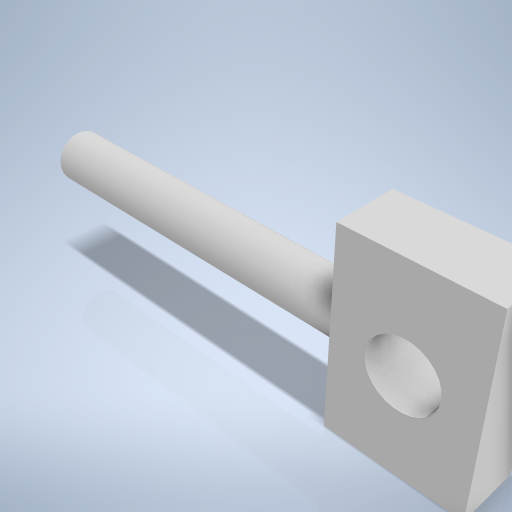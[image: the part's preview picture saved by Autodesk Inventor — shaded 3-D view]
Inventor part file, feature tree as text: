
AUTODESK INVENTOR PART (.ipt)
format: ipt  version: 2024.2 (Build 282272000, 272)  size: 252,416 bytes
history: native  units: mm
features: sketch x4, extrude x2, hole x2
ambient origin geometry x8: Origin, YZ Plane, XZ Plane, XY Plane, X Axis, Y Axis, Z Axis, Center Point
bodies: Volumenkörper1 (feature_tree)
feature tree (8):
  extrude  "Extrusion1"  Depth=13.0mm
  hole  "Bohrung1"  [1 undecoded]
  extrude  "Extrusion2"  [1 undecoded]
  hole  "Bohrung2"  [1 undecoded]
  sketch  "Skizze2"  dims[d1=19.0mm d2=13.0mm]
  sketch  "Skizze3"  dims[d3=6.0mm d4=0.0mm]
  sketch  "Skizze4"  dims[d5=6.5mm d6=8.0mm d7=4.0mm d8=2.0mm d9=90.0deg d10=15.75mm d11=20.594885mm d12=5.0mm]
  sketch  "Skizze5"  dims[d13=34.0mm d14=0.0mm d15=3.242mm d16=5.0mm d17=4.0mm d18=2.0mm d19=90.0deg d20=5.0mm d21=0.0mm]
note: 3 required parameter values undecoded (feature->parameter linkage not recoverable at this tier; creation-order binding heuristic only, values carry confidence <= 0.55)
